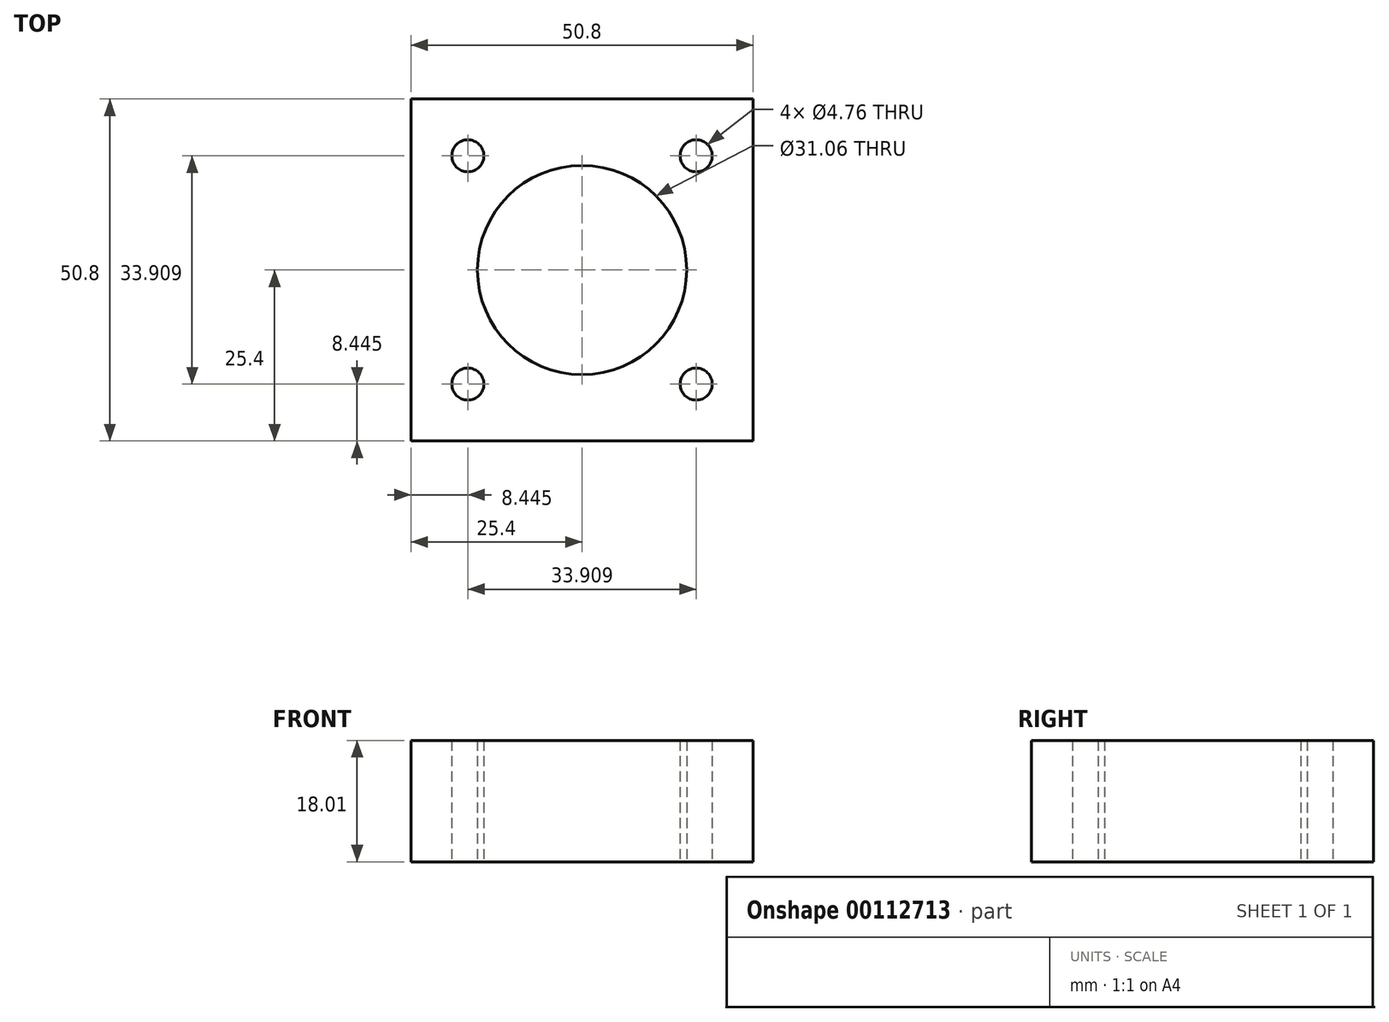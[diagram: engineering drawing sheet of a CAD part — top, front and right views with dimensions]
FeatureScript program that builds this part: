
annotation { "Feature Type Name" : "Feature", "Feature Type Description" : "" }
export const myFeature = defineFeature(function(context is Context, id is Id, definition is map)
    precondition{}
    {
        {
            var Q0;
            Q0=qCreatedBy(makeId("Top.planeOp"),FACE);
            var sketch = newSketch(context, id + "F0", { "sketchPlane" : qUnion([Q0])});
            skLineSegment(sketch, "E0.bottom", {"start": v(25.4, -25.4) * mm, "end": v(-25.4, -25.4) * mm});
            skLineSegment(sketch, "E0.top", {"start": v(25.4, 25.4) * mm, "end": v(-25.4, 25.4) * mm});
            skLineSegment(sketch, "E0.left", {"start": v(25.4, -25.4) * mm, "end": v(25.4, 25.4) * mm});
            skLineSegment(sketch, "E0.right", {"start": v(-25.4, -25.4) * mm, "end": v(-25.4, 25.4) * mm});
            skPoint(sketch, "E0.middle", {"position": v(0, 0) * mm});
            skLineSegment(sketch, "E1.bottom", {"start": v(16.95, 16.95) * mm, "end": v(-16.95, 16.95) * mm, "construction": true});
            skLineSegment(sketch, "E1.top", {"start": v(16.95, -16.95) * mm, "end": v(-16.95, -16.95) * mm, "construction": true});
            skLineSegment(sketch, "E1.left", {"start": v(16.95, 16.95) * mm, "end": v(16.95, -16.95) * mm, "construction": true});
            skLineSegment(sketch, "E1.right", {"start": v(-16.95, 16.95) * mm, "end": v(-16.95, -16.95) * mm, "construction": true});
            skCircle(sketch, "E2", {"center": v(0, 0) * mm, "radius": 15.53 * mm});
            skCircle(sketch, "E3", {"center": v(-16.95, 16.95) * mm, "radius": 8.45 * mm, "construction": true});
            skCircle(sketch, "E4", {"center": v(-16.95, 16.95) * mm, "radius": 2.38 * mm});
            skCircle(sketch, "E5", {"center": v(16.95, 16.95) * mm, "radius": 2.38 * mm});
            skCircle(sketch, "E6", {"center": v(-16.95, -16.95) * mm, "radius": 2.38 * mm});
            skCircle(sketch, "E7", {"center": v(16.95, -16.95) * mm, "radius": 2.38 * mm});
            skSolve(sketch);
        }
        {
            var Q0;
            Q0=qSketchRegion(id+"F0",true);
            extrude(context, id + "F1", {"entities" : qUnion([Q0]), "depth" : 18 * mm});
        }
    });
